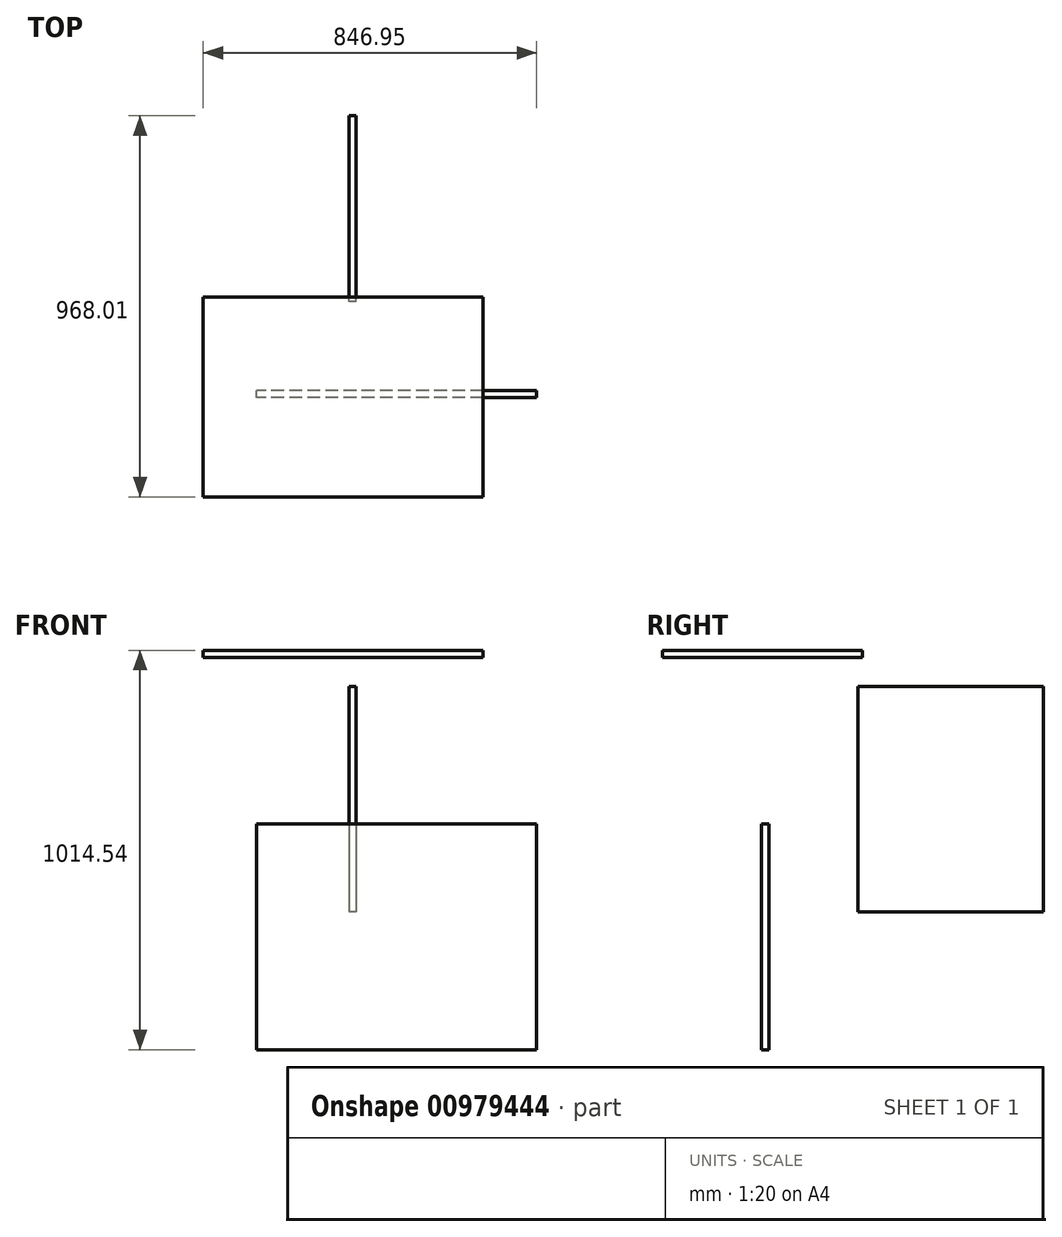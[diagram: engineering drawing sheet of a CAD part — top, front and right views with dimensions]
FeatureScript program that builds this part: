
annotation { "Feature Type Name" : "Feature", "Feature Type Description" : "" }
export const myFeature = defineFeature(function(context is Context, id is Id, definition is map)
    precondition{}
    {
        {
            var Q0;
            Q0=qCreatedBy(makeId("Top.planeOp"),FACE);
            var sketch = newSketch(context, id + "F0", { "sketchPlane" : qUnion([Q0])});
            skLineSegment(sketch, "E0.bottom", {"start": v(-370.37, 237.73) * mm, "end": v(340.83, 237.73) * mm});
            skLineSegment(sketch, "E0.top", {"start": v(-370.37, -270.27) * mm, "end": v(340.83, -270.27) * mm});
            skLineSegment(sketch, "E0.left", {"start": v(-370.37, 237.73) * mm, "end": v(-370.37, -270.27) * mm});
            skLineSegment(sketch, "E0.right", {"start": v(340.83, 237.73) * mm, "end": v(340.83, -270.27) * mm});
            skSolve(sketch);
        }
        {
            var Q0;
            Q0=makeQuery(id+"F0.imprint","IMPRINT",FACE,{"disambiguationData":[TD([[makeQuery(id+"F0.imprint","IMPRINT",EDGE,{"derivedFrom":sQuery(id+"F0.wireOp",EDGE,"E0.bottom")}),-1.0]])]});
            extrude(context, id + "F1", {"entities" : qUnion([Q0]), "depth" : 18.26 * mm, "offsetDistance" : 25.4 * mm});
        }
        {
            var Q0;
            Q0=qCreatedBy(makeId("Front.planeOp"),FACE);
            var sketch = newSketch(context, id + "F2", { "sketchPlane" : qUnion([Q0])});
            skLineSegment(sketch, "E1.bottom", {"start": v(476.58, -423.26) * mm, "end": v(-234.62, -423.26) * mm});
            skLineSegment(sketch, "E1.top", {"start": v(476.58, -996.28) * mm, "end": v(-234.62, -996.28) * mm});
            skLineSegment(sketch, "E1.left", {"start": v(476.58, -423.26) * mm, "end": v(476.58, -996.28) * mm});
            skLineSegment(sketch, "E1.right", {"start": v(-234.62, -423.26) * mm, "end": v(-234.62, -996.28) * mm});
            skSolve(sketch);
        }
        {
            var Q0;
            Q0 = qSketchRegion(id + "F2", true);
            extrude(context, id + "F3", {"entities" : qUnion([Q0]), "depth" : 18.26 * mm, "offsetDistance" : 25.4 * mm});
        }
        {
            var Q0;
            Q0=qCreatedBy(makeId("Right.planeOp"),FACE);
            var sketch = newSketch(context, id + "F4", { "sketchPlane" : qUnion([Q0])});
            skLineSegment(sketch, "E2.bottom", {"start": v(226.32, -73.32) * mm, "end": v(697.74, -73.32) * mm});
            skLineSegment(sketch, "E2.top", {"start": v(226.32, -646.35) * mm, "end": v(697.74, -646.35) * mm});
            skLineSegment(sketch, "E2.left", {"start": v(226.32, -73.32) * mm, "end": v(226.32, -646.35) * mm});
            skLineSegment(sketch, "E2.right", {"start": v(697.74, -73.32) * mm, "end": v(697.74, -646.35) * mm});
            skSolve(sketch);
        }
        {
            var Q0;
            Q0 = qSketchRegion(id + "F4", true);
            extrude(context, id + "F5", {"entities" : qUnion([Q0]), "depth" : 18.26 * mm, "offsetDistance" : 25.4 * mm});
        }
    });
